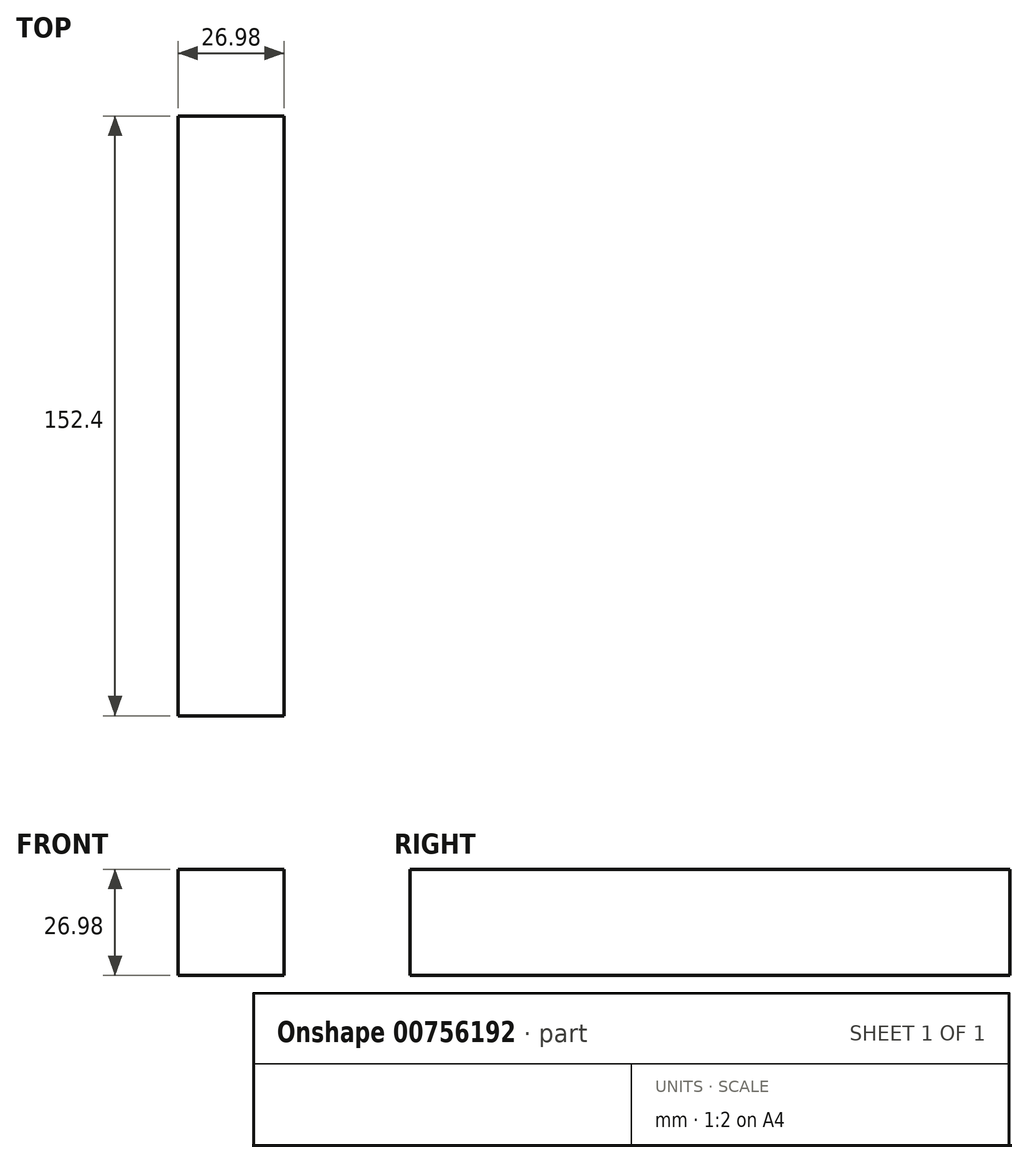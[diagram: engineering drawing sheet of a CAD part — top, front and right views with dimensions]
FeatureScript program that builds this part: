
annotation { "Feature Type Name" : "Feature", "Feature Type Description" : "" }
export const myFeature = defineFeature(function(context is Context, id is Id, definition is map)
    precondition{}
    {
        {
            var Q0;
            Q0=qCreatedBy(makeId("Front.planeOp"),FACE);
            var sketch = newSketch(context, id + "F0", { "sketchPlane" : qUnion([Q0])});
            skLineSegment(sketch, "E0.bottom", {"start": v(13.5, 13.5) * mm, "end": v(-13.5, 13.5) * mm});
            skLineSegment(sketch, "E0.top", {"start": v(13.5, -13.5) * mm, "end": v(-13.5, -13.5) * mm});
            skLineSegment(sketch, "E0.left", {"start": v(13.5, 13.5) * mm, "end": v(13.5, -13.5) * mm});
            skLineSegment(sketch, "E0.right", {"start": v(-13.5, 13.5) * mm, "end": v(-13.5, -13.5) * mm});
            skPoint(sketch, "E0.middle", {"position": v(0, 0) * mm});
            skSolve(sketch);
        }
        {
            var Q0;
            Q0 = qSketchRegion(id + "F0", true);
            extrude(context, id + "F1", {"entities" : qUnion([Q0]), "depth" : 152.4 * mm, "offsetDistance" : 25.4 * mm});
        }
    });
